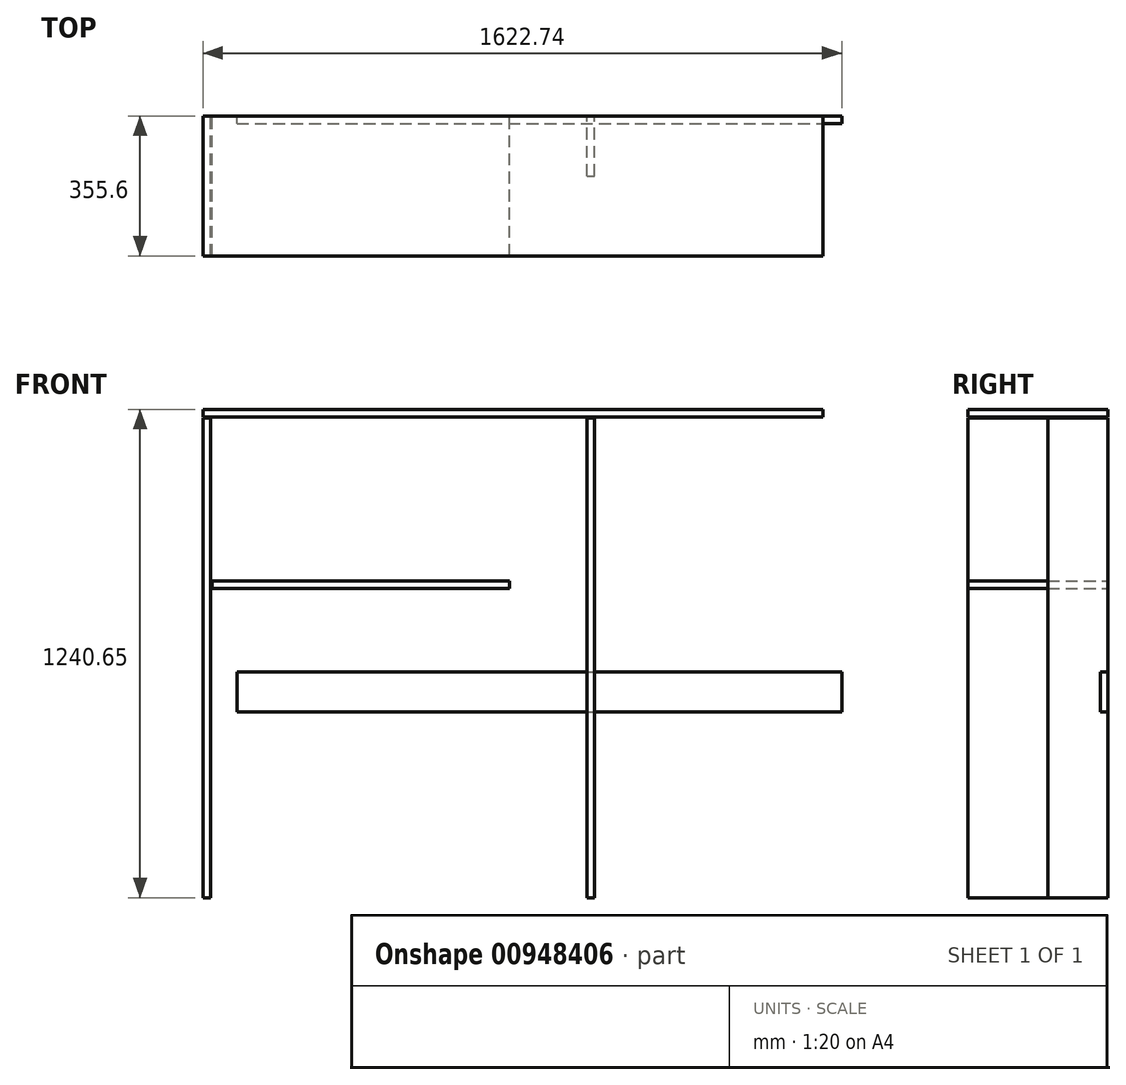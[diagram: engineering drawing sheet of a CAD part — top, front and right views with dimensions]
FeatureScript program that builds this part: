
annotation { "Feature Type Name" : "Feature", "Feature Type Description" : "" }
export const myFeature = defineFeature(function(context is Context, id is Id, definition is map)
    precondition{}
    {
        {
            var Q0;
            Q0=qCreatedBy(makeId("Front.planeOp"),FACE);
            var sketch = newSketch(context, id + "F0", { "sketchPlane" : qUnion([Q0])});
            skLineSegment(sketch, "E0.bottom", {"start": v(0, 0) * mm, "end": v(19.05, 0) * mm});
            skLineSegment(sketch, "E0.top", {"start": v(0, 1219.2) * mm, "end": v(19.05, 1219.2) * mm});
            skLineSegment(sketch, "E0.left", {"start": v(0, 0) * mm, "end": v(0, 1219.2) * mm});
            skLineSegment(sketch, "E0.right", {"start": v(19.05, 0) * mm, "end": v(19.05, 1219.2) * mm});
            skSolve(sketch);
        }
        {
            var Q0;
            Q0 = qSketchRegion(id + "F0", true);
            extrude(context, id + "F1", {"entities" : qUnion([Q0]), "depth" : 355.6 * mm, "offsetDistance" : 25.4 * mm});
        }
        {
            var Q0;
            Q0=qCreatedBy(makeId("Front.planeOp"),FACE);
            var sketch = newSketch(context, id + "F2", { "sketchPlane" : qUnion([Q0])});
            skLineSegment(sketch, "E1.bottom", {"start": v(0, 1240.65) * mm, "end": v(1574.8, 1240.65) * mm});
            skLineSegment(sketch, "E1.top", {"start": v(0, 1221.6) * mm, "end": v(1574.8, 1221.6) * mm});
            skLineSegment(sketch, "E1.left", {"start": v(0, 1240.65) * mm, "end": v(0, 1221.6) * mm});
            skLineSegment(sketch, "E1.right", {"start": v(1574.8, 1240.65) * mm, "end": v(1574.8, 1221.6) * mm});
            skSolve(sketch);
        }
        {
            var Q0;
            Q0 = qSketchRegion(id + "F2", true);
            extrude(context, id + "F3", {"entities" : qUnion([Q0]), "depth" : 355.6 * mm, "offsetDistance" : 25.4 * mm});
        }
        {
            var Q0;
            Q0=qCreatedBy(makeId("Front.planeOp"),FACE);
            var sketch = newSketch(context, id + "F4", { "sketchPlane" : qUnion([Q0])});
            skLineSegment(sketch, "E2.bottom", {"start": v(23.21, 804.86) * mm, "end": v(778.86, 804.86) * mm});
            skLineSegment(sketch, "E2.top", {"start": v(23.21, 785.8) * mm, "end": v(778.86, 785.8) * mm});
            skLineSegment(sketch, "E2.left", {"start": v(23.21, 804.86) * mm, "end": v(23.21, 785.8) * mm});
            skLineSegment(sketch, "E2.right", {"start": v(778.86, 804.86) * mm, "end": v(778.86, 785.8) * mm});
            skSolve(sketch);
        }
        {
            var Q0;
            Q0 = qSketchRegion(id + "F4", true);
            extrude(context, id + "F5", {"entities" : qUnion([Q0]), "depth" : 355.6 * mm, "offsetDistance" : 25.4 * mm});
        }
        {
            var Q0;
            Q0=qCreatedBy(makeId("Front.planeOp"),FACE);
            var sketch = newSketch(context, id + "F6", { "sketchPlane" : qUnion([Q0])});
            skLineSegment(sketch, "E3.bottom", {"start": v(86.04, 572.9) * mm, "end": v(1622.74, 572.9) * mm});
            skLineSegment(sketch, "E3.top", {"start": v(86.04, 471.3) * mm, "end": v(1622.74, 471.3) * mm});
            skLineSegment(sketch, "E3.left", {"start": v(86.04, 572.9) * mm, "end": v(86.04, 471.3) * mm});
            skLineSegment(sketch, "E3.right", {"start": v(1622.74, 572.9) * mm, "end": v(1622.74, 471.3) * mm});
            skSolve(sketch);
        }
        {
            var Q0;
            Q0 = qSketchRegion(id + "F6", true);
            extrude(context, id + "F7", {"entities" : qUnion([Q0]), "depth" : 19.05 * mm, "offsetDistance" : 25.4 * mm});
        }
        {
            var Q0;
            Q0=qCreatedBy(makeId("Front.planeOp"),FACE);
            var sketch = newSketch(context, id + "F8", { "sketchPlane" : qUnion([Q0])});
            skLineSegment(sketch, "E4.bottom", {"start": v(975.14, 1219.2) * mm, "end": v(994.19, 1219.2) * mm});
            skLineSegment(sketch, "E4.top", {"start": v(975.14, 0) * mm, "end": v(994.19, 0) * mm});
            skLineSegment(sketch, "E4.left", {"start": v(975.14, 1219.2) * mm, "end": v(975.14, 0) * mm});
            skLineSegment(sketch, "E4.right", {"start": v(994.19, 1219.2) * mm, "end": v(994.19, 0) * mm});
            skSolve(sketch);
        }
        {
            var Q0;
            Q0 = qSketchRegion(id + "F8", true);
            extrude(context, id + "F9", {"entities" : qUnion([Q0]), "depth" : 152.4 * mm, "offsetDistance" : 25.4 * mm});
        }
    });
